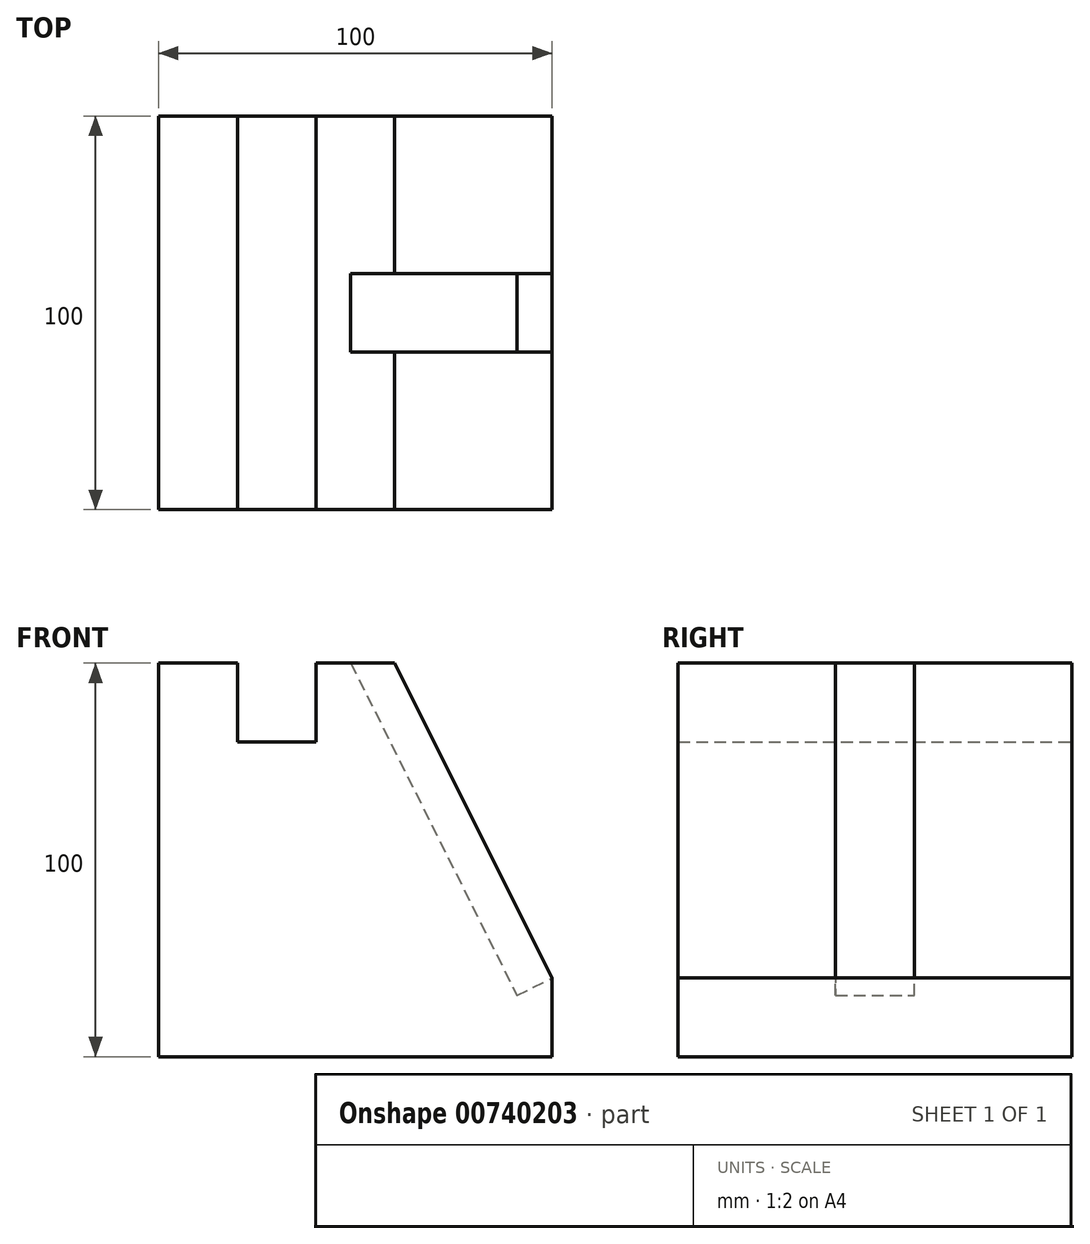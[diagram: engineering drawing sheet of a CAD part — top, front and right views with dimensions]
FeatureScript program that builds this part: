
annotation { "Feature Type Name" : "Feature", "Feature Type Description" : "" }
export const myFeature = defineFeature(function(context is Context, id is Id, definition is map)
    precondition{}
    {
        {
            var Q0;
            Q0=qCreatedBy(makeId("Front.planeOp"),FACE);
            var sketch = newSketch(context, id + "F0", { "sketchPlane" : qUnion([Q0])});
            skLineSegment(sketch, "E0", {"start": v(0, 0) * mm, "end": v(0, -100) * mm});
            skLineSegment(sketch, "E1", {"start": v(0, -100) * mm, "end": v(100, -100) * mm});
            skLineSegment(sketch, "E2", {"start": v(100, -100) * mm, "end": v(100, -80) * mm});
            skLineSegment(sketch, "E3", {"start": v(0, 0) * mm, "end": v(20, 0) * mm});
            skLineSegment(sketch, "E4", {"start": v(20, 0) * mm, "end": v(20, -20) * mm});
            skLineSegment(sketch, "E5", {"start": v(20, -20) * mm, "end": v(40, -20) * mm});
            skLineSegment(sketch, "E6", {"start": v(40, -20) * mm, "end": v(40, 0) * mm});
            skLineSegment(sketch, "E7", {"start": v(40, 0) * mm, "end": v(60, 0) * mm});
            skLineSegment(sketch, "E8", {"start": v(60, 0) * mm, "end": v(100, -80) * mm});
            skSolve(sketch);
        }
        {
            var Q0;
            Q0=makeQuery(id+"F0.imprint","IMPRINT",FACE,{"disambiguationData":[TD([[makeQuery(id+"F0.imprint","IMPRINT",EDGE,{"derivedFrom":sQuery(id+"F0.wireOp",EDGE,"E0")}),1.0]])]});
            extrude(context, id + "F1", {"entities" : qUnion([Q0]), "depth" : 100 * mm, "offsetDistance" : 25 * mm});
        }
        {
            var Q0;
            Q0=makeQuery(id+"F1.opExtrude","SWEPT_FACE",FACE,{"disambiguationData":[OSD([sQuery(id+"F0.wireOp",EDGE,"E8")])]});
            var sketch = newSketch(context, id + "F2", { "sketchPlane" : qUnion([Q0])});
            skLineSegment(sketch, "E9", {"start": v(-100, -26.83) * mm, "end": v(-60, -26.83) * mm});
            skLineSegment(sketch, "E10", {"start": v(-60, -26.83) * mm, "end": v(-40, -26.83) * mm});
            skLineSegment(sketch, "E11", {"start": v(-40, -26.83) * mm, "end": v(0, -26.83) * mm});
            skLineSegment(sketch, "E12", {"start": v(-60, -26.83) * mm, "end": v(-60, -116.28) * mm});
            skLineSegment(sketch, "E13", {"start": v(-60, -116.28) * mm, "end": v(-40, -116.28) * mm});
            skLineSegment(sketch, "E14", {"start": v(-40, -116.28) * mm, "end": v(-40, -26.83) * mm});
            skSolve(sketch);
        }
        {
            var Q0;
            Q0=makeQuery(id+"F2.imprint","IMPRINT",FACE,{"disambiguationData":[TD([[makeQuery(id+"F2.imprint","IMPRINT",EDGE,{"derivedFrom":sQuery(id+"F2.wireOp",EDGE,"E12")}),1.0]])]});
            extrude(context, id + "F3", {"entities" : qUnion([Q0]), "operationType" : NewBodyOperationType.REMOVE, "oppositeDirection" : true, "depth" : 10 * mm, "offsetDistance" : 25 * mm});
        }
        {
            var Q0;
            Q0=makeQuery(id+"F3.boolean.opBoolean","COPY",FACE,{"derivedFrom":makeQuery(id+"F3.opExtrude","SWEPT_FACE",FACE,{"disambiguationData":[OSD([sQuery(id+"F2.wireOp",EDGE,"E10")])]})});
            extrude(context, id + "F4", {"entities" : qUnion([Q0]), "operationType" : NewBodyOperationType.REMOVE, "oppositeDirection" : true, "depth" : 10 * mm, "offsetDistance" : 25 * mm});
        }
    });
